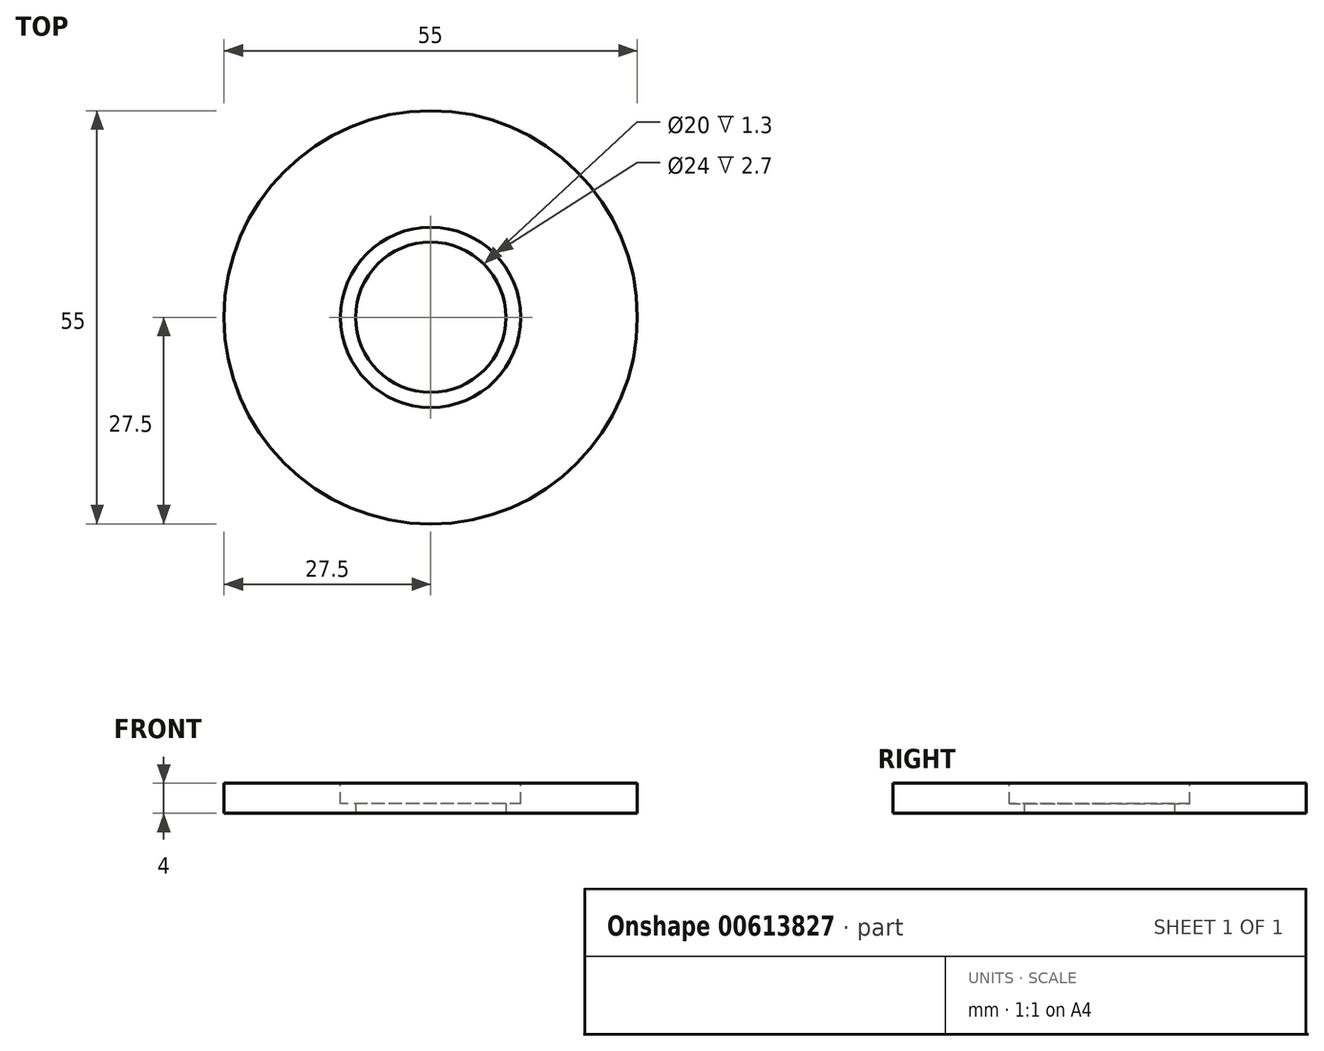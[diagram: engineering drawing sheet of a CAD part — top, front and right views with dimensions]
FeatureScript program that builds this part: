
annotation { "Feature Type Name" : "Feature", "Feature Type Description" : "" }
export const myFeature = defineFeature(function(context is Context, id is Id, definition is map)
    precondition{}
    {
        {
            var Q0;
            Q0=qCreatedBy(makeId("Top.planeOp"),FACE);
            var sketch = newSketch(context, id + "F0", { "sketchPlane" : qUnion([Q0])});
            skCircle(sketch, "E0", {"center": v(0, 0) * mm, "radius": 27.5 * mm});
            skCircle(sketch, "E1", {"center": v(0, 0) * mm, "radius": 10 * mm});
            skSolve(sketch);
        }
        {
            var Q0;
            Q0 = qSketchRegion(id + "F0", true);
            extrude(context, id + "F1", {"entities" : qUnion([Q0]), "depth" : 4 * mm, "offsetDistance" : 25 * mm});
        }
        {
            var Q0;
            Q0=makeQuery(id+"F1.opExtrude","CAP_FACE",FACE,{"disambiguationData":[OSD([sQuery(id+"F0.wireOp",EDGE,"E0"),sQuery(id+"F0.wireOp",EDGE,"E1")])],"isStart":false});
            var sketch = newSketch(context, id + "F2", { "sketchPlane" : qUnion([Q0])});
            skCircle(sketch, "E2", {"center": v(0, 0) * mm, "radius": 12 * mm});
            skSolve(sketch);
        }
        {
            var Q0;
            Q0=makeQuery(id+"F2.imprint","IMPRINT",FACE,{"disambiguationData":[TD([[makeQuery(id+"F2.imprint","IMPRINT",EDGE,{"derivedFrom":sQuery(id+"F2.wireOp",EDGE,"E2")}),1.0]])]});
            extrude(context, id + "F3", {"entities" : qUnion([Q0]), "operationType" : NewBodyOperationType.REMOVE, "oppositeDirection" : true, "depth" : 2.7 * mm, "offsetDistance" : 25 * mm});
        }
    });
